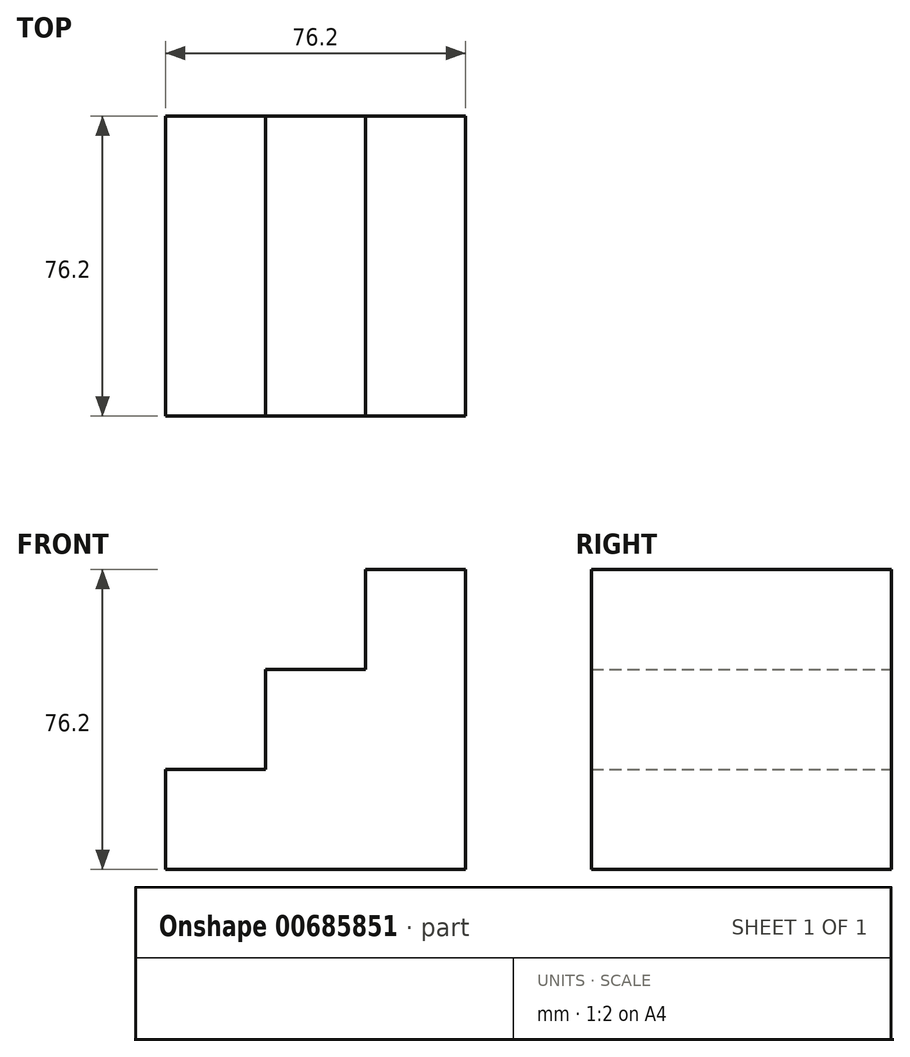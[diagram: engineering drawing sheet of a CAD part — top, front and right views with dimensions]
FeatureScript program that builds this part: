
annotation { "Feature Type Name" : "Feature", "Feature Type Description" : "" }
export const myFeature = defineFeature(function(context is Context, id is Id, definition is map)
    precondition{}
    {
        {
            var Q0;
            Q0=qCreatedBy(makeId("Front.planeOp"),FACE);
            var sketch = newSketch(context, id + "F0", { "sketchPlane" : qUnion([Q0])});
            skLineSegment(sketch, "E0", {"start": v(0, 0) * mm, "end": v(-76.2, 0) * mm});
            skLineSegment(sketch, "E1", {"start": v(0, 0) * mm, "end": v(0, 76.2) * mm});
            skLineSegment(sketch, "E2", {"start": v(-76.2, 0) * mm, "end": v(-76.2, 25.4) * mm});
            skLineSegment(sketch, "E3", {"start": v(-76.2, 25.4) * mm, "end": v(-50.8, 25.4) * mm});
            skLineSegment(sketch, "E4", {"start": v(-50.8, 25.4) * mm, "end": v(-50.8, 50.8) * mm});
            skLineSegment(sketch, "E5", {"start": v(-50.8, 50.8) * mm, "end": v(-25.4, 50.8) * mm});
            skLineSegment(sketch, "E6", {"start": v(-25.4, 50.8) * mm, "end": v(-25.4, 76.2) * mm});
            skLineSegment(sketch, "E7", {"start": v(0, 76.2) * mm, "end": v(-25.4, 76.2) * mm});
            skSolve(sketch);
        }
        {
            var Q0;
            Q0 = qSketchRegion(id + "F0", true);
            extrude(context, id + "F1", {"entities" : qUnion([Q0]), "depth" : 76.2 * mm, "offsetDistance" : 25.4 * mm});
        }
    });
